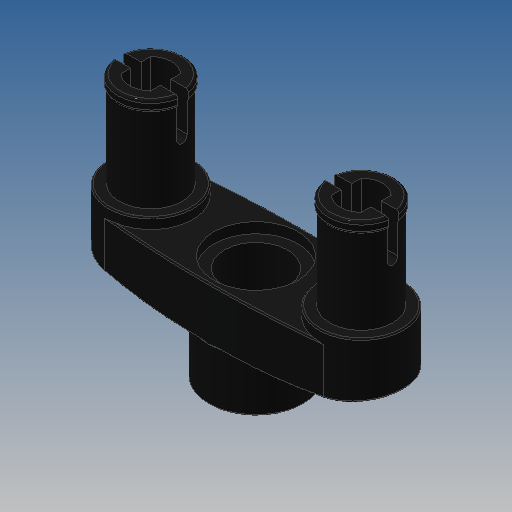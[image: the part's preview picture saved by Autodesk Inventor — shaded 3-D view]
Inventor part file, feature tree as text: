
AUTODESK INVENTOR PART (.ipt)
format: ipt  version: 2022.2 (Build 262287000, 287)  size: 407,552 bytes
history: native  units: in
note: dims shown in document units (in); Inventor stores cm internally (conversion verified against a paired STEP export)
features: sketch x5, extrude x5, revolve x2, mirror x1, fillet x1
ambient origin geometry x8: Origin, YZ Plane, XZ Plane, XY Plane, X Axis, Y Axis, Z Axis, Center Point
bodies: Solid1 (feature_tree)
feature tree (14):
  sketch  "Sketch2"  dims[d0=0.252in d1=0.6299in]
  extrude  "Extrusion1"  Depth=0.6299in
  extrude  "Extrusion2"  Depth=0.189in
  sketch  "Sketch4"  dims[d4=0.2835in d5=0.1575in]
  extrude  "Extrusion3"  Depth=0.1575in
  revolve  "Revolution1"  [1 undecoded]
  revolve  "Revolution2"  [1 undecoded]
  extrude  "Extrusion5"  Depth=0.0079in
  extrude  "Extrusion4"  Depth=0.0079in
  mirror  "Mirror1"
  fillet  "Fillet1"  Radius=0.0315in
  sketch  "Sketch3"  dims[d2=0.252in d3=0.189in]
  sketch  "Sketch5"  dims[d6=0.0in d7=0.042in]
  sketch  "Sketch6"  dims[d8=0.1102in d9=0.0in d10=0.315in d11=0.1969in d12=0.189in d14=0.0315in d15=0.0315in d16=0.189in d17=0.0315in d18=0.252in d19=0.2835in d20=0.315in d21=0.126in d22=0.126in d23=0.1102in d24=0.0in d25=90.0deg d26=90.0deg d27=0.0315in d28=0.1339in d29=0.1102in d30=0.0in d33=0.126in d34=45.0deg d35=0.1102in d36=0.0in d37=0.0039in d39=0.0in d41=0.0in d42=0.0in d43=0.0in d44=0.0in d45=0.0079in]
note: 2 required parameter values undecoded (feature->parameter linkage not recoverable at this tier; creation-order binding heuristic only, values carry confidence <= 0.55)
